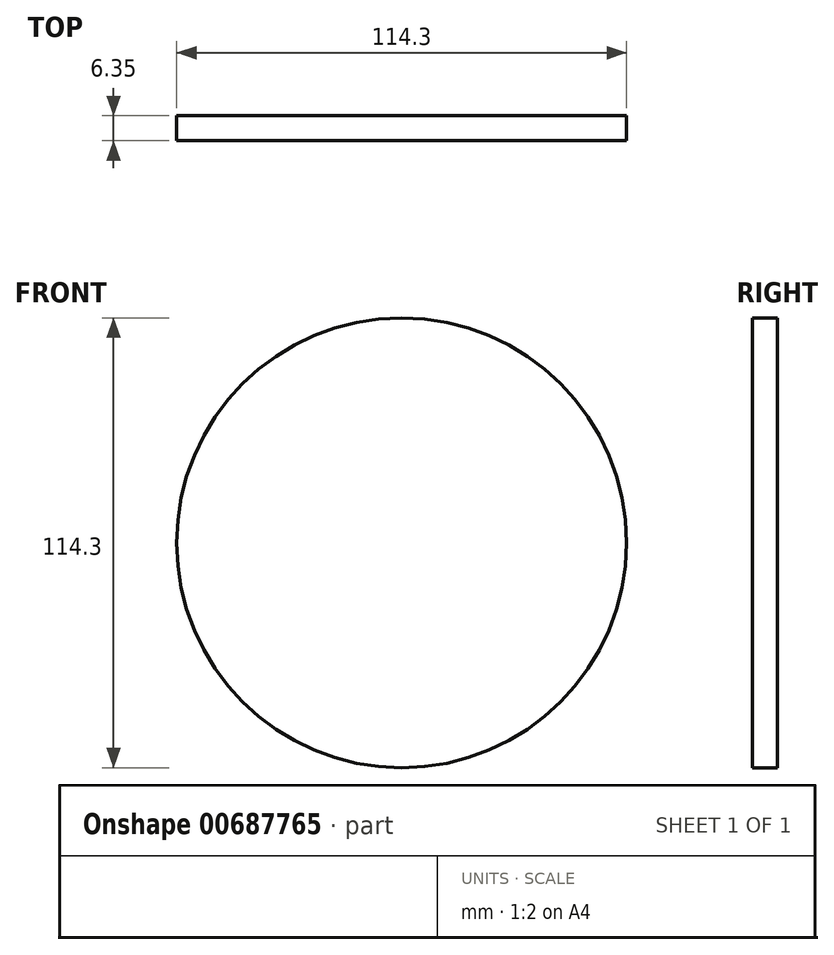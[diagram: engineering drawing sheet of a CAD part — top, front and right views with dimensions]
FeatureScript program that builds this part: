
annotation { "Feature Type Name" : "Feature", "Feature Type Description" : "" }
export const myFeature = defineFeature(function(context is Context, id is Id, definition is map)
    precondition{}
    {
        {
            var Q0;
            Q0=qCreatedBy(makeId("Front.planeOp"),FACE);
            var sketch = newSketch(context, id + "F0", { "sketchPlane" : qUnion([Q0])});
            skCircle(sketch, "E0", {"center": v(0, 0) * mm, "radius": 63.5 * mm});
            skCircle(sketch, "E1", {"center": v(0, 0) * mm, "radius": 57.15 * mm});
            skSolve(sketch);
        }
        {
            var Q0;
            Q0=makeQuery(id+"F0.imprint","IMPRINT",FACE,{"disambiguationData":[TD([[makeQuery(id+"F0.imprint","IMPRINT",EDGE,{"derivedFrom":sQuery(id+"F0.wireOp",EDGE,"E1")}),1.0]])]});
            extrude(context, id + "F1", {"entities" : qUnion([Q0]), "oppositeDirection" : true, "depth" : 6.35 * mm, "offsetDistance" : 25.4 * mm});
        }
    });
